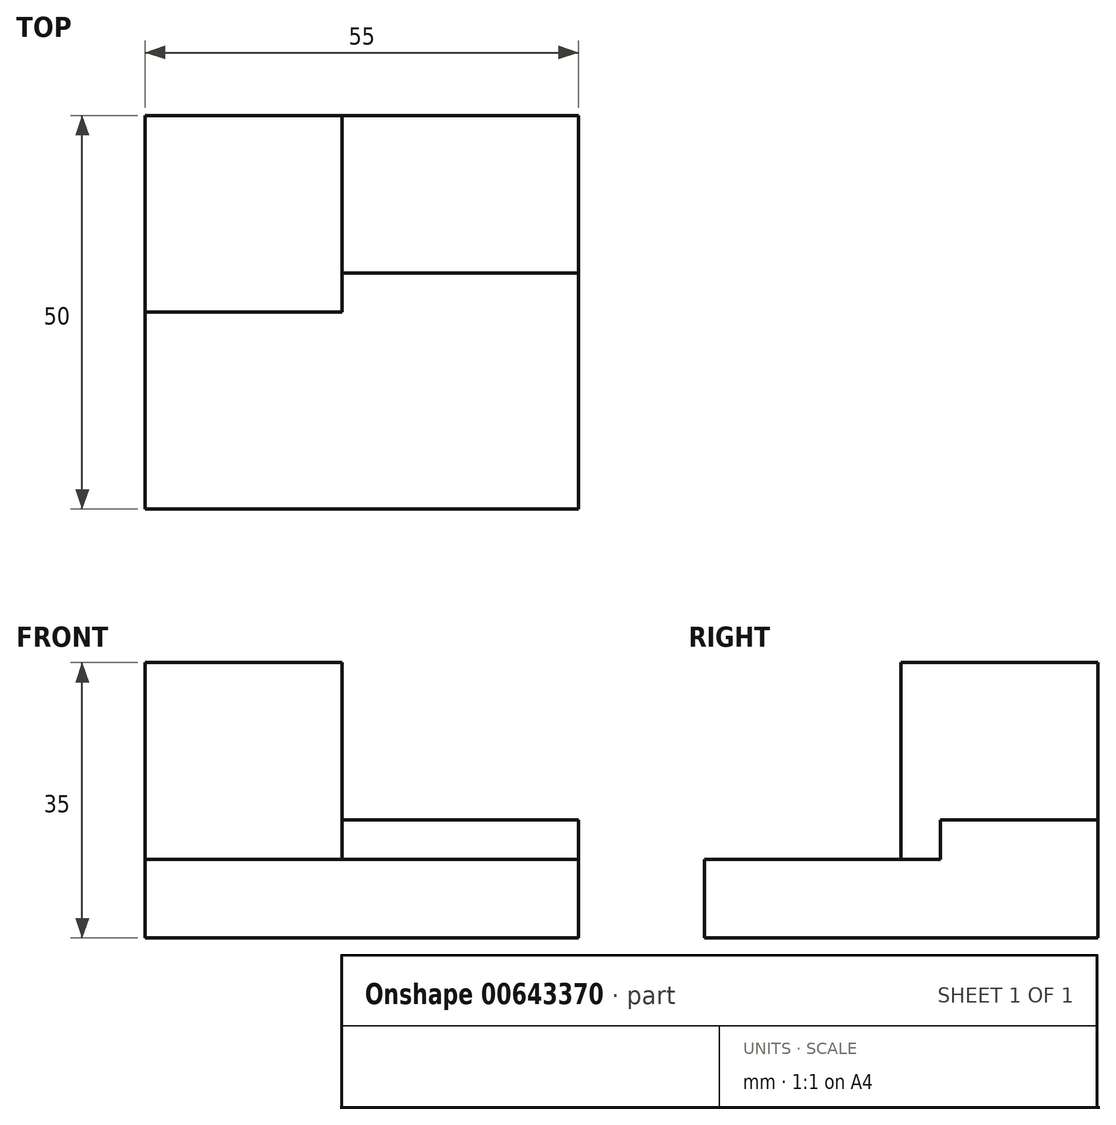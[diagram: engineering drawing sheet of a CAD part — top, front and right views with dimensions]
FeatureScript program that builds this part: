
annotation { "Feature Type Name" : "Feature", "Feature Type Description" : "" }
export const myFeature = defineFeature(function(context is Context, id is Id, definition is map)
    precondition{}
    {
        {
            var Q0;
            Q0=qCreatedBy(makeId("Front.planeOp"),FACE);
            var sketch = newSketch(context, id + "F0", { "sketchPlane" : qUnion([Q0])});
            skLineSegment(sketch, "E0.bottom", {"start": v(-27.5, 5) * mm, "end": v(27.5, 5) * mm});
            skLineSegment(sketch, "E0.top", {"start": v(-27.5, -5) * mm, "end": v(27.5, -5) * mm});
            skLineSegment(sketch, "E0.left", {"start": v(-27.5, 5) * mm, "end": v(-27.5, -5) * mm});
            skLineSegment(sketch, "E0.right", {"start": v(27.5, 5) * mm, "end": v(27.5, -5) * mm});
            skPoint(sketch, "E0.middle", {"position": v(0, 0) * mm});
            skSolve(sketch);
        }
        {
            var Q0;
            Q0 = qSketchRegion(id + "F0", true);
            extrude(context, id + "F1", {"entities" : qUnion([Q0]), "depth" : 50 * mm, "offsetDistance" : 25 * mm});
        }
        {
            var Q0;
            Q0=makeQuery(id+"F1.opExtrude","SWEPT_FACE",FACE,{"disambiguationData":[OSD([sQuery(id+"F0.wireOp",EDGE,"E0.bottom")])]});
            var sketch = newSketch(context, id + "F2", { "sketchPlane" : qUnion([Q0])});
            skLineSegment(sketch, "E1.bottom", {"start": v(-27.5, 0) * mm, "end": v(-2.5, 0) * mm});
            skLineSegment(sketch, "E1.top", {"start": v(-27.5, -25) * mm, "end": v(-2.5, -25) * mm});
            skLineSegment(sketch, "E1.left", {"start": v(-27.5, 0) * mm, "end": v(-27.5, -25) * mm});
            skLineSegment(sketch, "E1.right", {"start": v(-2.5, 0) * mm, "end": v(-2.5, -25) * mm});
            skSolve(sketch);
        }
        {
            var Q0;
            Q0=makeQuery(id+"F1.opExtrude","SWEPT_FACE",FACE,{"disambiguationData":[OSD([sQuery(id+"F0.wireOp",EDGE,"E0.right")])]});
            var sketch = newSketch(context, id + "F3", { "sketchPlane" : qUnion([Q0])});
            skLineSegment(sketch, "E2.bottom", {"start": v(0, -5) * mm, "end": v(-20, -5) * mm});
            skLineSegment(sketch, "E2.top", {"start": v(0, 10) * mm, "end": v(-20, 10) * mm});
            skLineSegment(sketch, "E2.left", {"start": v(0, -5) * mm, "end": v(0, 10) * mm});
            skLineSegment(sketch, "E2.right", {"start": v(-20, -5) * mm, "end": v(-20, 10) * mm});
            skSolve(sketch);
        }
        {
            var Q0;
            Q0 = qSketchRegion(id + "F3", true);
            extrude(context, id + "F4", {"entities" : qUnion([Q0]), "operationType" : NewBodyOperationType.ADD, "oppositeDirection" : true, "depth" : 55 * mm, "offsetDistance" : 25 * mm});
        }
        {
            var Q0;
            Q0 = qSketchRegion(id + "F2", true);
            extrude(context, id + "F5", {"entities" : qUnion([Q0]), "operationType" : NewBodyOperationType.ADD, "depth" : 25 * mm, "offsetDistance" : 25 * mm});
        }
    });
